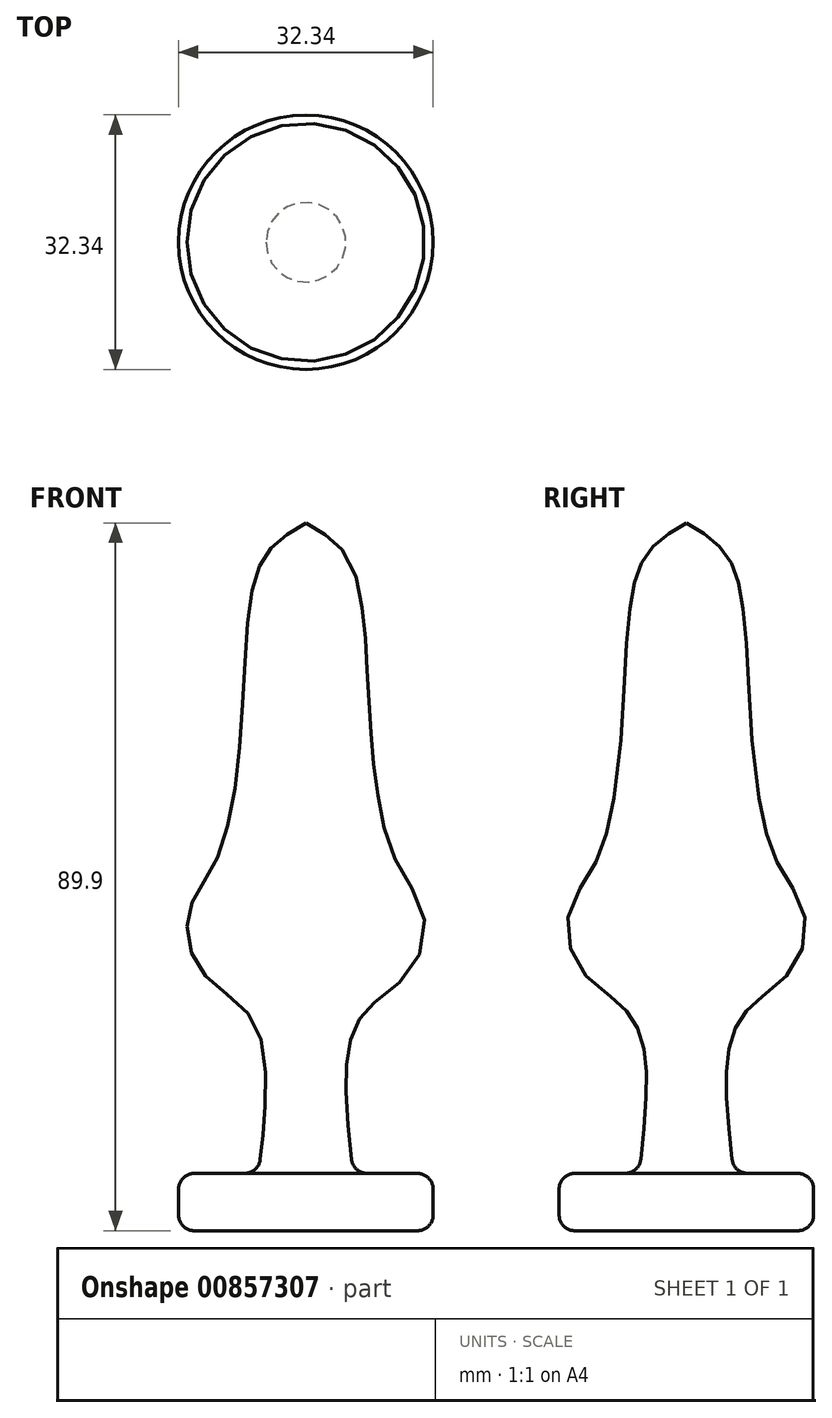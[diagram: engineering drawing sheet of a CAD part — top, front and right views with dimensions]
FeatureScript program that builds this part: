
annotation { "Feature Type Name" : "Feature", "Feature Type Description" : "" }
export const myFeature = defineFeature(function(context is Context, id is Id, definition is map)
    precondition{}
    {
        {
            var Q0;
            Q0=qCreatedBy(makeId("Front.planeOp"),FACE);
            var sketch = newSketch(context, id + "F0", { "sketchPlane" : qUnion([Q0])});
            skFitSpline(sketch, "E0", {"points": [v(0, 67.58) * mm, v(-4.37, 64.45) * mm, v(-6.89, 58.62) * mm, v(-8.28, 40.8) * mm, v(-11.41, 24.7) * mm, v(-14.89, 18.18) * mm, v(-13.24, 10.61) * mm, v(-6.63, 4.26) * mm, v(-5.23, -7.48) * mm, v(-6.02, -15.05) * mm], "startDerivative": vector(-57.62, -33.46) * mm, "endDerivative": vector(-8.56, -68.93) * mm});
            skLineSegment(sketch, "E1", {"start": v(-6.02, -15.05) * mm, "end": v(-16.17, -15.05) * mm});
            skLineSegment(sketch, "E2", {"start": v(-16.17, -15.05) * mm, "end": v(-16.17, -22.32) * mm});
            skLineSegment(sketch, "E3", {"start": v(-16.17, -22.32) * mm, "end": v(0, -22.32) * mm});
            skLineSegment(sketch, "E4", {"start": v(0, -22.32) * mm, "end": v(0, 67.58) * mm});
            skSolve(sketch);
        }
        {
            var Q0;
            Q0=makeQuery(id+"F0.imprint","IMPRINT",FACE,{"disambiguationData":[TD([[makeQuery(id+"F0.imprint","IMPRINT",EDGE,{"derivedFrom":sQuery(id+"F0.wireOp",EDGE,"E0")}),1.0]])]});
            var Q1;
            Q1=sQuery(id+"F0.wireOp",EDGE,"E4");
            revolve(context, id + "F1", {"surfaceOperationType" : NewSurfaceOperationType.NEW, "entities" : qUnion([Q0]), "axis" : qUnion([Q1]), "revolveType" : RevolveType.FULL});
        }
        {
            var Q0;
            Q0=makeQuery(id+"F1.opRevolve","SWEPT_EDGE",EDGE,{"disambiguationData":[OSD([sQuery(id+"F0.wireOp",EDGE,"E1"),sQuery(id+"F0.wireOp",EDGE,"E2")])]});
            var Q1;
            Q1=makeQuery(id+"F1.opRevolve","SWEPT_EDGE",EDGE,{"disambiguationData":[OSD([sQuery(id+"F0.wireOp",EDGE,"E2"),sQuery(id+"F0.wireOp",EDGE,"E3")])]});
            fillet(context, id + "F2", {"entities" : qUnion([Q0, Q1]), "radius" : 2 * mm, "tangentPropagation" : true, "allowEdgeOverflow" : false});
        }
        {
            var Q0;
            Q0=makeQuery(id+"F1.opRevolve","SWEPT_EDGE",EDGE,{"disambiguationData":[OSD([sQuery(id+"F0.wireOp",EDGE,"E0"),sQuery(id+"F0.wireOp",EDGE,"E1")])]});
            fillet(context, id + "F3", {"entities" : qUnion([Q0]), "radius" : 2 * mm, "tangentPropagation" : true, "allowEdgeOverflow" : false});
        }
    });
